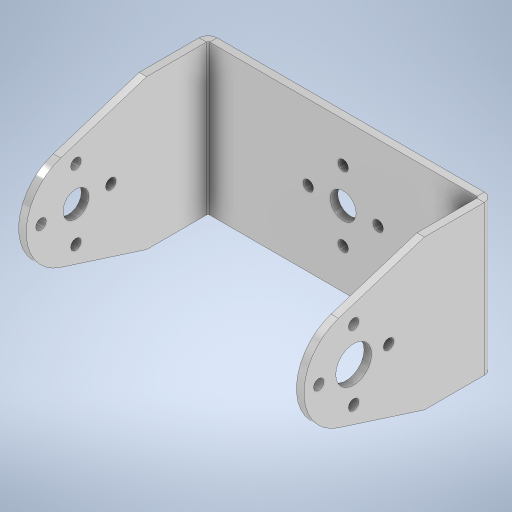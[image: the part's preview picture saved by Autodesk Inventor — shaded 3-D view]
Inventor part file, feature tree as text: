
AUTODESK INVENTOR PART (.ipt)
format: ipt  version: 2024.2 (Build 282272000, 272)  size: 308,736 bytes
history: native  units: in
note: dims shown in document units (in); Inventor stores cm internally (conversion verified against a paired STEP export)
features: sketch x7, other x7, reference x6, sheet_metal_op x4, hole x1, extrude x1
ambient origin geometry x8: Origin, YZ Plane, XZ Plane, XY Plane, X Axis, Y Axis, Z Axis, Center Point
bodies: Solid1 (feature_tree)
feature tree (26):
  sheet_metal_op  "Face1"
  sheet_metal_op  "Flange1"
  hole  "Hole1"  [1 undecoded]
  extrude  "Extrusion1"  Depth=0.0591in
  sketch  "Sketch1"  dims[d0=2.2512in d1=1.1811in]
  other  "Plate1"
  sketch  "Sketch2"  dims[d2=0.0591in d3=0.0591in]
  other  "Plate2"
  sheet_metal_op  "Bend1"
  sheet_metal_op  "Corner1"
  sketch  "Sketch3"  dims[d4=0.0295in]
  sketch  "Sketch4"  dims[d5=0.1181in]
  reference  "Reference1"
  reference  "Reference2"
  reference  "Reference3"
  reference  "Reference4"
  reference  "Reference5"
  sketch  "Sketch5"  dims[d6=0.0122in]
  reference  "Reference6"
  sketch  "Sketch12"  dims[d7=1.7717in d8=90.0deg d9=0.0122in]
  sketch  "Sketch13"  dims[d10=0.2362in d11=0.0591in d12=0.0122in d13=0.7843in d14=0.4724in d15=1.1024in d16=2.2512in d17=0.0in d19=0.0827in d20=0.2362in d21=0.1575in d22=0.0787in d23=90.0deg d24=0.0591in d25=0.0in d26=0.2047in d27=0.0in d28=0.0in d52=0.2047in d53=0.0827in d54=0.2756in d55=1.5748in d57=360.0deg d59=2.2512in d60=0.0in d61=0.2835in d62=0.0591in d63=0.0in]
  other  "Cut1"
  other  "Cut5"
  other  "Cut6"
  other  "2_Arm.iam"
  other  "Top Horn:4"
note: 1 required parameter value undecoded (feature->parameter linkage not recoverable at this tier; creation-order binding heuristic only, values carry confidence <= 0.55)
